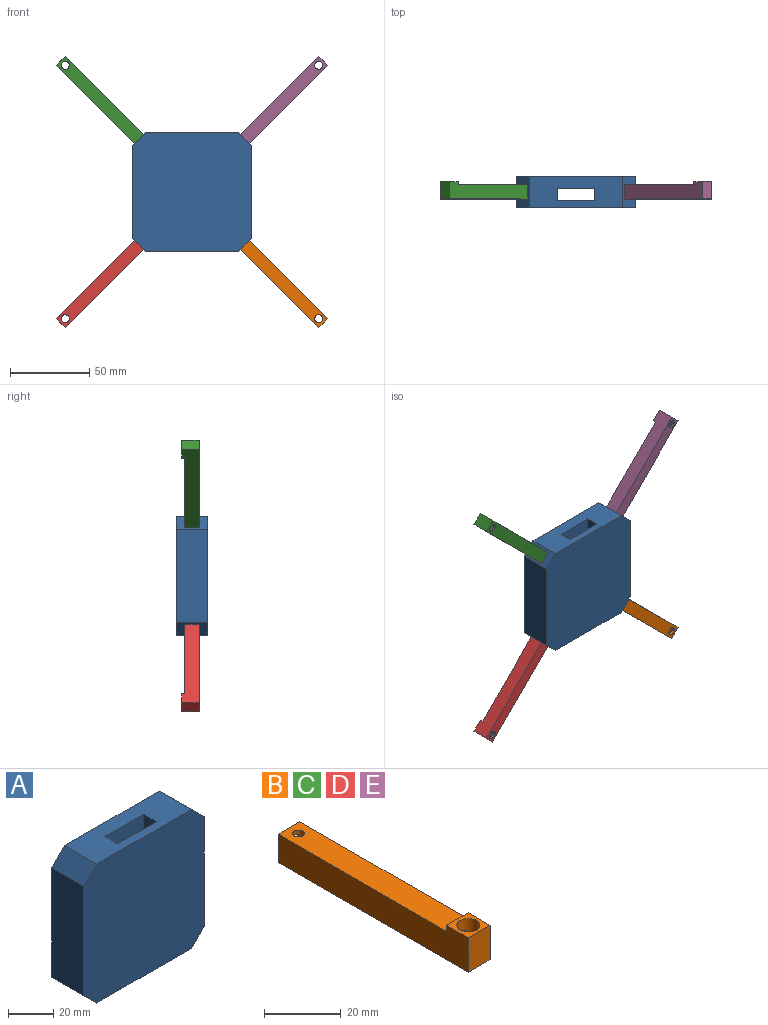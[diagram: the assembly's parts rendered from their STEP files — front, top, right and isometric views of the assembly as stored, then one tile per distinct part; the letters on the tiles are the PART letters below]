
ASSEMBLY  parts=5 mates=4
PART A: 25 faces, bbox 75x20x75 mm
  f0: plane 75x75mm, normal (0,1,0), area 3422mm2, adj f1,f2,f3,f5,f6,f8,f9,f10
  f1: plane 17.5x9mm, normal (0,0,1), area 147.9mm2, adj f0,f9,f12,f17,f18,f24
  f2: plane 59x20mm, normal (0,0,-1), area 988mm2, adj f0,f7,f13,f14,f17,f18,f19,f20
  f3: plane 59x20mm, normal (0,0,1), area 988mm2, adj f0,f7,f15,f16,f18,f19,f20,f21
  f4: plane 45x10.5mm, normal (0,1,0), area 472.5mm2, adj f8,f10,f11,f19
  f5: plane 59x20mm, normal (1,0,0), area 1180mm2, adj f0,f7,f13,f16
  f6: plane 59x20mm, normal (-1,0,0), area 1180mm2, adj f0,f7,f14,f15
  f7: plane 75x75mm, normal (0,-1,0), area 5497mm2, adj f2,f3,f5,f6,f13,f14,f15,f16
  f8: plane 17.5x9mm, normal (0,0,1), area 147.9mm2, adj f0,f4,f11,f17,f19,f23
  f9: plane 45x9mm, normal (-1,0,0), area 405mm2, adj f0,f1,f10,f12
  f10: plane 45x9mm, normal (0,0,-1), area 372.1mm2, adj f0,f4,f9,f11,f12,f18,f19,f21
  f11: plane 45x9mm, normal (1,0,0), area 405mm2, adj f0,f4,f8,f10
  f12: plane 45x10.5mm, normal (0,1,0), area 472.5mm2, adj f1,f9,f10,f18
  f13: plane 20x8mm, normal (0.71,0,-0.71), area 226.3mm2, adj f0,f2,f5,f7
  f14: plane 20x8mm, normal (-0.71,0,-0.71), area 226.3mm2, adj f0,f2,f6,f7
  f15: plane 20x8mm, normal (-0.71,0,0.71), area 226.3mm2, adj f0,f3,f6,f7
  f16: plane 20x8mm, normal (0.71,0,0.71), area 226.3mm2, adj f0,f3,f5,f7
  f17: plane 24x15mm, normal (0,-1,0), area 310mm2, adj f1,f2,f8,f18,f19,f22,f23,f24
  f18: plane 75x8mm, normal (-1,0,0), area 538.4mm2, adj f1,f2,f3,f10,f12,f17,f20,f21
  f19: plane 75x8mm, normal (1,0,0), area 538.4mm2, adj f2,f3,f4,f8,f10,f17,f20,f21
  f20: plane 75x24mm, normal (0,1,0), area 1800mm2, adj f2,f3,f18,f19
  f21: plane 24x15mm, normal (0,-1,0), area 360mm2, adj f3,f10,f18,f19
  f22: plane 10x7.63mm, normal (0,0,1), area 76.3mm2, adj f0,f17,f23,f24
  f23: plane 7.63x5mm, normal (1,0,0), area 38.2mm2, adj f0,f8,f17,f22
  f24: plane 7.63x5mm, normal (-1,0,0), area 38.2mm2, adj f0,f1,f17,f22
PART B: 16 faces, bbox 8x70x11 mm
  f0: plane 70x8mm, normal (0,0,-1), area 540.4mm2, adj f1,f3,f4,f5,f11
  f1: plane 70x11mm, normal (1,0,0), area 646mm2, adj f0,f2,f4,f5,f6,f7
  f2: plane 62x8mm, normal (0,0,1), area 488.5mm2, adj f1,f3,f5,f6,f15
  f3: plane 70x11mm, normal (-1,0,0), area 646mm2, adj f0,f2,f4,f5,f6,f7
  f4: plane 11x8mm, normal (0,-1,0), area 88mm2, adj f0,f1,f3,f7
  f5: plane 9x8mm, normal (0,1,0), area 40.3mm2, adj f0,f1,f2,f3,f14
  f6: plane 8x2mm, normal (0,1,0), area 16mm2, adj f1,f2,f3,f7
  f7: plane 8x8mm, normal (0,0,1), area 35.7mm2, adj f1,f3,f4,f6,f9
  f8: cylinder r=3mm len=2.27mm, axis (0,0,1), area 2.1mm2, adj f9,f10,f14
  f9: cylinder r=3mm len=9mm, axis (0,0,1), area 123.3mm2, adj f7,f8,f10,f12,f13,f14
  f10: plane 6x5.27mm, normal (0,0,1), area 6.5mm2, adj f8,f9,f11,f14
  f11: cylinder r=2.5mm len=5mm, axis (0,0,-1), area 29.5mm2, adj f0,f10,f14
  f12: plane 2.64x0.29mm, normal (0,1,0), area 0.5mm2, adj f9,f14
  f13: plane 2.64x0.29mm, normal (0,1,0), area 0.5mm2, adj f9,f14
  f14: cylinder r=3.18mm len=66.8mm, axis (0,1,0), area 1282.3mm2, adj f5,f8,f9,f10,f11,f12,f13,f15
  f15: cylinder r=1.55mm len=3.09mm, axis (0,0,1), area 14.8mm2, adj f2,f14
PART C: same geometry as B
PART D: same geometry as B
PART E: same geometry as B
PLACE A t=(-34.18,-11.3,-2.35)mm
PLACE B rot(axis=(-0.28,0.68,0.68),148.6deg) t=(-3.51,-25.8,-38.68)mm
PLACE C rot(axis=(-0.86,-0.36,-0.36),98.4deg) t=(-64.85,-25.8,33.98)mm
PLACE D rot(axis=(-0.28,-0.68,-0.68),148.6deg) t=(-70.51,-25.8,-33.02)mm
PLACE E rot(axis=(-0.86,0.36,0.36),98.4deg) t=(2.15,-25.8,28.32)mm
MATE fastened B.f14 <-> A.f13  axis (-0.71,0,0.71) through (-0.68,-21.3,-35.85)mm
MATE fastened D.f14 <-> A.f14  axis (0.71,0,0.71) through (-67.68,-21.3,-35.85)mm
MATE fastened E.f14 <-> A.f16  axis (-0.71,0,-0.71) through (-0.68,-21.3,31.15)mm
MATE fastened C.f14 <-> A.f15  axis (0.71,0,-0.71) through (-67.68,-21.3,31.15)mm
